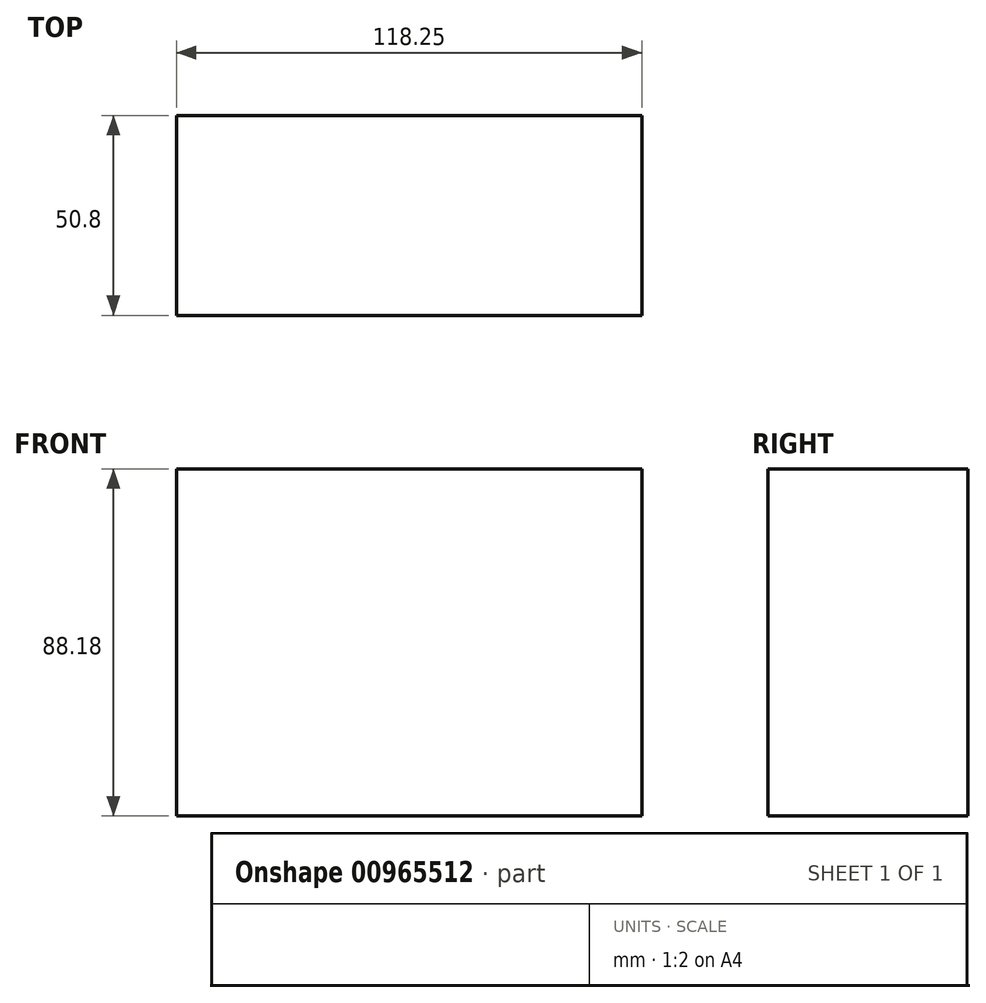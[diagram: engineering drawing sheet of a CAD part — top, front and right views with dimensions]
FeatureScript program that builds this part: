
annotation { "Feature Type Name" : "Feature", "Feature Type Description" : "" }
export const myFeature = defineFeature(function(context is Context, id is Id, definition is map)
    precondition{}
    {
        {
            var Q0;
            Q0=qCreatedBy(makeId("Front.planeOp"),FACE);
            var sketch = newSketch(context, id + "F0", { "sketchPlane" : qUnion([Q0])});
            skLineSegment(sketch, "E0.bottom", {"start": v(-63.27, -38.17) * mm, "end": v(54.98, -38.17) * mm});
            skLineSegment(sketch, "E0.top", {"start": v(-63.27, 50) * mm, "end": v(54.98, 50) * mm});
            skLineSegment(sketch, "E0.left", {"start": v(-63.27, -38.17) * mm, "end": v(-63.27, 50) * mm});
            skLineSegment(sketch, "E0.right", {"start": v(54.98, -38.17) * mm, "end": v(54.98, 50) * mm});
            skSolve(sketch);
        }
        {
            var Q0;
            Q0=makeQuery(id+"F0.imprint","IMPRINT",FACE,{"disambiguationData":[TD([[makeQuery(id+"F0.imprint","IMPRINT",EDGE,{"derivedFrom":sQuery(id+"F0.wireOp",EDGE,"E0.bottom")}),1.0]])]});
            extrude(context, id + "F1", {"entities" : qUnion([Q0]), "depth" : 50.8 * mm, "offsetDistance" : 25.4 * mm});
        }
    });
